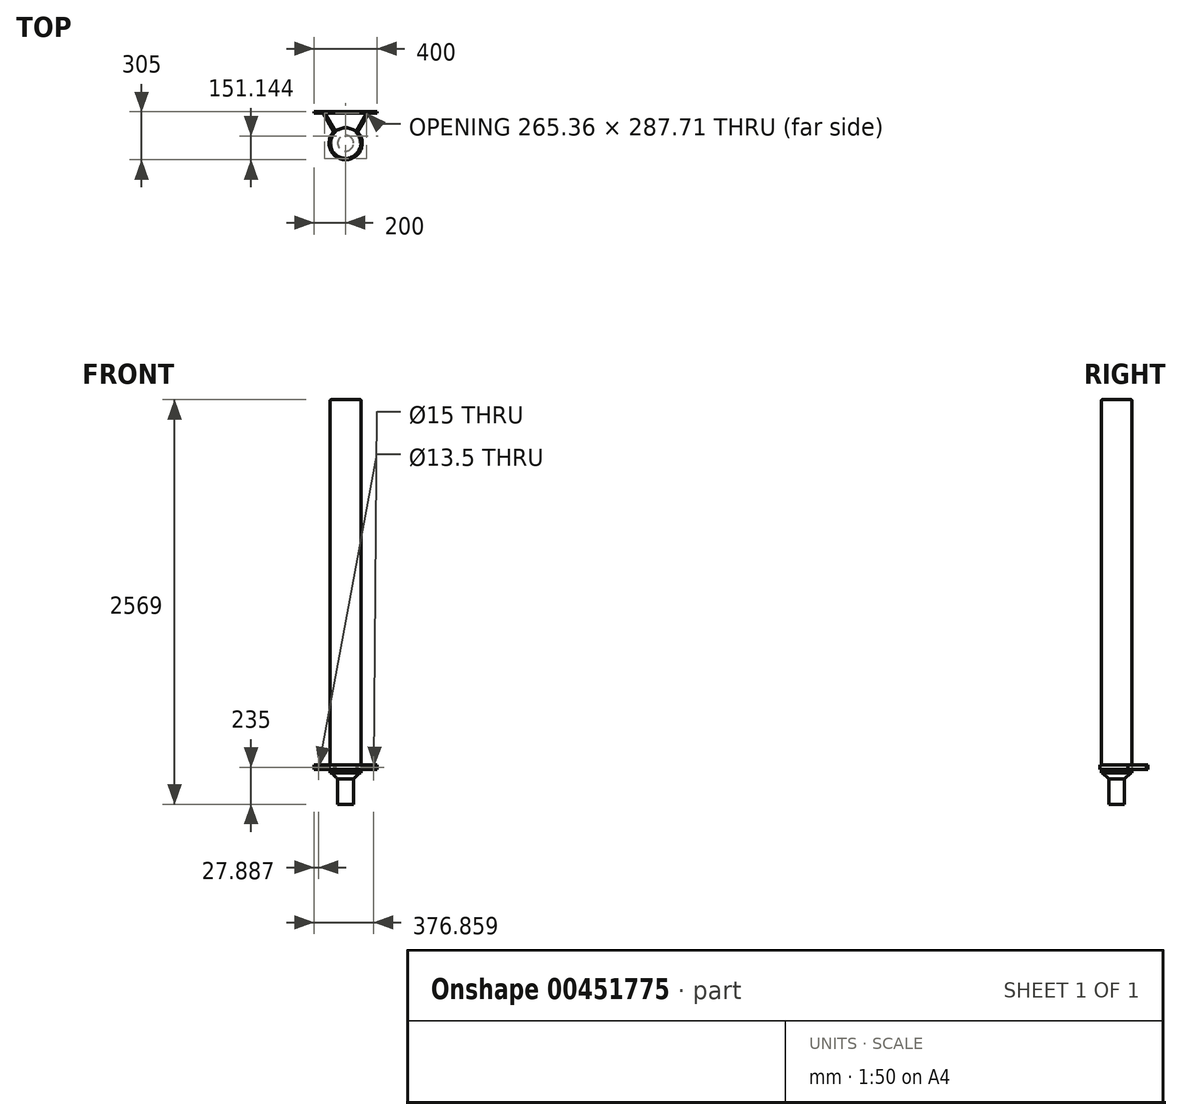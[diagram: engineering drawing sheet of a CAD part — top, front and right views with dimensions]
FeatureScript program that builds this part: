
annotation { "Feature Type Name" : "Feature", "Feature Type Description" : "" }
export const myFeature = defineFeature(function(context is Context, id is Id, definition is map)
    precondition{}
    {
        {
            var Q0;
            Q0=qCreatedBy(makeId("Top.planeOp"),FACE);
            var sketch = newSketch(context, id + "F0", { "sketchPlane" : qUnion([Q0])});
            skCircle(sketch, "E0", {"center": v(0, 0) * mm, "radius": 98 * mm});
            skSolve(sketch);
        }
        {
            var Q0;
            Q0=makeQuery(id+"F0.imprint","IMPRINT",FACE,{"disambiguationData":[TD([[makeQuery(id+"F0.imprint","IMPRINT",EDGE,{"derivedFrom":sQuery(id+"F0.wireOp",EDGE,"E0")}),1.0]])]});
            extrude(context, id + "F1", {"entities" : qUnion([Q0]), "endBound" : BoundingType.SYMMETRIC, "depth" : 2569 * mm});
        }
        {
            var Q0;
            Q0=makeQuery(id+"F1.opExtrude","CAP_FACE",FACE,{"disambiguationData":[OSD([sQuery(id+"F0.wireOp",EDGE,"E0")])],"isStart":true});
            var sketch = newSketch(context, id + "F2", { "sketchPlane" : qUnion([Q0])});
            skCircle(sketch, "E1", {"center": v(0, 0) * mm, "radius": 50 * mm});
            skCircle(sketch, "E2.0", {"center": v(0, 0) * mm, "radius": 98 * mm});
            skSolve(sketch);
        }
        {
            var Q0;
            Q0=makeQuery(id+"F2.imprint","IMPRINT",FACE,{"disambiguationData":[TD([[makeQuery(id+"F2.imprint","IMPRINT",EDGE,{"derivedFrom":sQuery(id+"F2.wireOp",EDGE,"E1")}),-1.0]])]});
            extrude(context, id + "F3", {"entities" : qUnion([Q0]), "operationType" : NewBodyOperationType.REMOVE, "oppositeDirection" : true, "depth" : 200 * mm});
        }
        {
            var Q0;
            Q0=makeQuery(id+"F3.boolean.opBoolean","COPY",EDGE,{"derivedFrom":makeQuery(id+"F3.opExtrude","CAP_EDGE",EDGE,{"disambiguationData":[OSD([sQuery(id+"F2.wireOp",EDGE,"E1")])],"isStart":false})});
            chamfer(context, id + "F4", {"entities" : qUnion([Q0]), "width" : 40 * mm, "tangentPropagation" : true});
        }
        {
            var Q0;
            Q0=makeQuery(id+"F3.boolean.opBoolean","COPY",EDGE,{"derivedFrom":makeQuery(id+"F3.opExtrude","CAP_EDGE",EDGE,{"disambiguationData":[OSD([sQuery(id+"F2.wireOp",EDGE,"E1")])],"isStart":true})});
            var Q1;
            Q1=makeQuery(id+"F1.opExtrude","CAP_EDGE",EDGE,{"disambiguationData":[OSD([sQuery(id+"F0.wireOp",EDGE,"E0")])],"isStart":false});
            fillet(context, id + "F5", {"entities" : qUnion([Q0, Q1]), "radius" : 5 * mm, "tangentPropagation" : true, "allowEdgeOverflow" : false});
        }
        {
            var Q0;
            Q0=makeQuery(id+"F1.opExtrude","CAP_FACE",FACE,{"disambiguationData":[OSD([sQuery(id+"F0.wireOp",EDGE,"E0")])],"isStart":true});
            cPlane(context, id + "F6", {"entities" : qUnion([Q0]), "cplaneType" : CPlaneType.OFFSET, "offset" : 220 * mm, "oppositeDirection" : true, "width" : 150 * mm, "height" : 150 * mm});
        }
        {
            var Q0;
            Q0=qCreatedBy(id+"F6.planeOp",FACE);
            var sketch = newSketch(context, id + "F7", { "sketchPlane" : qUnion([Q0])});
            skArc(sketch, "E3.0", {"start": v(65.22, -73.15) * mm, "mid": v(0, 98) * mm, "end": v(-65.22, -73.15) * mm});
            skLineSegment(sketch, "E4", {"start": v(-65.22, -73.15) * mm, "end": v(-132.68, -190) * mm});
            skLineSegment(sketch, "E5", {"start": v(-132.68, -190) * mm, "end": v(132.68, -190) * mm});
            skLineSegment(sketch, "E6", {"start": v(132.68, -190) * mm, "end": v(65.22, -73.15) * mm});
            skArc(sketch, "E7", {"start": v(76.22, -72.22) * mm, "mid": v(0, 105) * mm, "end": v(-76.22, -72.22) * mm});
            skLineSegment(sketch, "E8", {"start": v(144.23, -190) * mm, "end": v(76.22, -72.22) * mm});
            skLineSegment(sketch, "E9", {"start": v(-76.22, -72.22) * mm, "end": v(-144.23, -190) * mm});
            skLineSegment(sketch, "E10", {"start": v(-150, -200) * mm, "end": v(150, -200) * mm});
            skLineSegment(sketch, "E11", {"start": v(-76.22, -72.22) * mm, "end": v(-65.22, -73.15) * mm});
            skLineSegment(sketch, "E12", {"start": v(76.22, -72.22) * mm, "end": v(65.22, -73.15) * mm});
            skLineSegment(sketch, "E13", {"start": v(-150, -200) * mm, "end": v(-200, -200) * mm});
            skLineSegment(sketch, "E14", {"start": v(-200, -200) * mm, "end": v(-200, -190) * mm});
            skLineSegment(sketch, "E15", {"start": v(-200, -190) * mm, "end": v(-144.23, -190) * mm});
            skLineSegment(sketch, "E16", {"start": v(150, -200) * mm, "end": v(200, -200) * mm});
            skLineSegment(sketch, "E17", {"start": v(200, -200) * mm, "end": v(200, -190) * mm});
            skLineSegment(sketch, "E18", {"start": v(200, -190) * mm, "end": v(144.23, -190) * mm});
            skSolve(sketch);
        }
        {
            var Q0;
            Q0=makeQuery(id+"F7.imprint","IMPRINT",FACE,{"disambiguationData":[TD([[makeQuery(id+"F7.imprint","IMPRINT",EDGE,{"derivedFrom":sQuery(id+"F7.wireOp",EDGE,"E4")}),-1.0]])]});
            var Q1;
            Q1=makeQuery(id+"F7.imprint","IMPRINT",FACE,{"disambiguationData":[TD([[makeQuery(id+"F7.imprint","IMPRINT",EDGE,{"derivedFrom":sQuery(id+"F7.wireOp",EDGE,"E3.0")}),-1.0]])]});
            extrude(context, id + "F8", {"entities" : qUnion([Q0, Q1]), "operationType" : NewBodyOperationType.ADD, "oppositeDirection" : true, "depth" : 30 * mm});
        }
        {
            var Q0;
            Q0=makeQuery(id+"F8.opExtrude","SWEPT_FACE",FACE,{"disambiguationData":[OSD([sQuery(id+"F7.wireOp",EDGE,"E15")])]});
            var sketch = newSketch(context, id + "F9", { "sketchPlane" : qUnion([Q0])});
            skCircle(sketch, "E19", {"center": v(-172.11, -1049.5) * mm, "radius": 6.75 * mm});
            skPoint(sketch, "E19.centerSnap0", {"position": v(-172.11, -1034.5) * mm});
            skPoint(sketch, "E19.centerSnap1", {"position": v(-200, -1049.5) * mm});
            skCircle(sketch, "E20", {"center": v(176.86, -1049.5) * mm, "radius": 7.5 * mm});
            skSolve(sketch);
        }
        {
            var Q0;
            Q0=makeQuery(id+"F9.imprint","IMPRINT",FACE,{"disambiguationData":[TD([[makeQuery(id+"F9.imprint","IMPRINT",EDGE,{"derivedFrom":sQuery(id+"F9.wireOp",EDGE,"E19")}),1.0]])]});
            var Q1;
            Q1=makeQuery(id+"F9.imprint","IMPRINT",FACE,{"disambiguationData":[TD([[makeQuery(id+"F9.imprint","IMPRINT",EDGE,{"derivedFrom":sQuery(id+"F9.wireOp",EDGE,"E20")}),1.0]])]});
            extrude(context, id + "F10", {"entities" : qUnion([Q0, Q1]), "operationType" : NewBodyOperationType.REMOVE, "endBound" : BoundingType.THROUGH_ALL, "oppositeDirection" : true, "depth" : 25 * mm});
        }
        {
            var Q0;
            Q0=qCreatedBy(id+"F6.planeOp",FACE);
            cPlane(context, id + "F11", {"entities" : qUnion([Q0]), "cplaneType" : CPlaneType.OFFSET, "offset" : 750 * mm, "oppositeDirection" : true, "width" : 150 * mm, "height" : 150 * mm});
        }
    });
